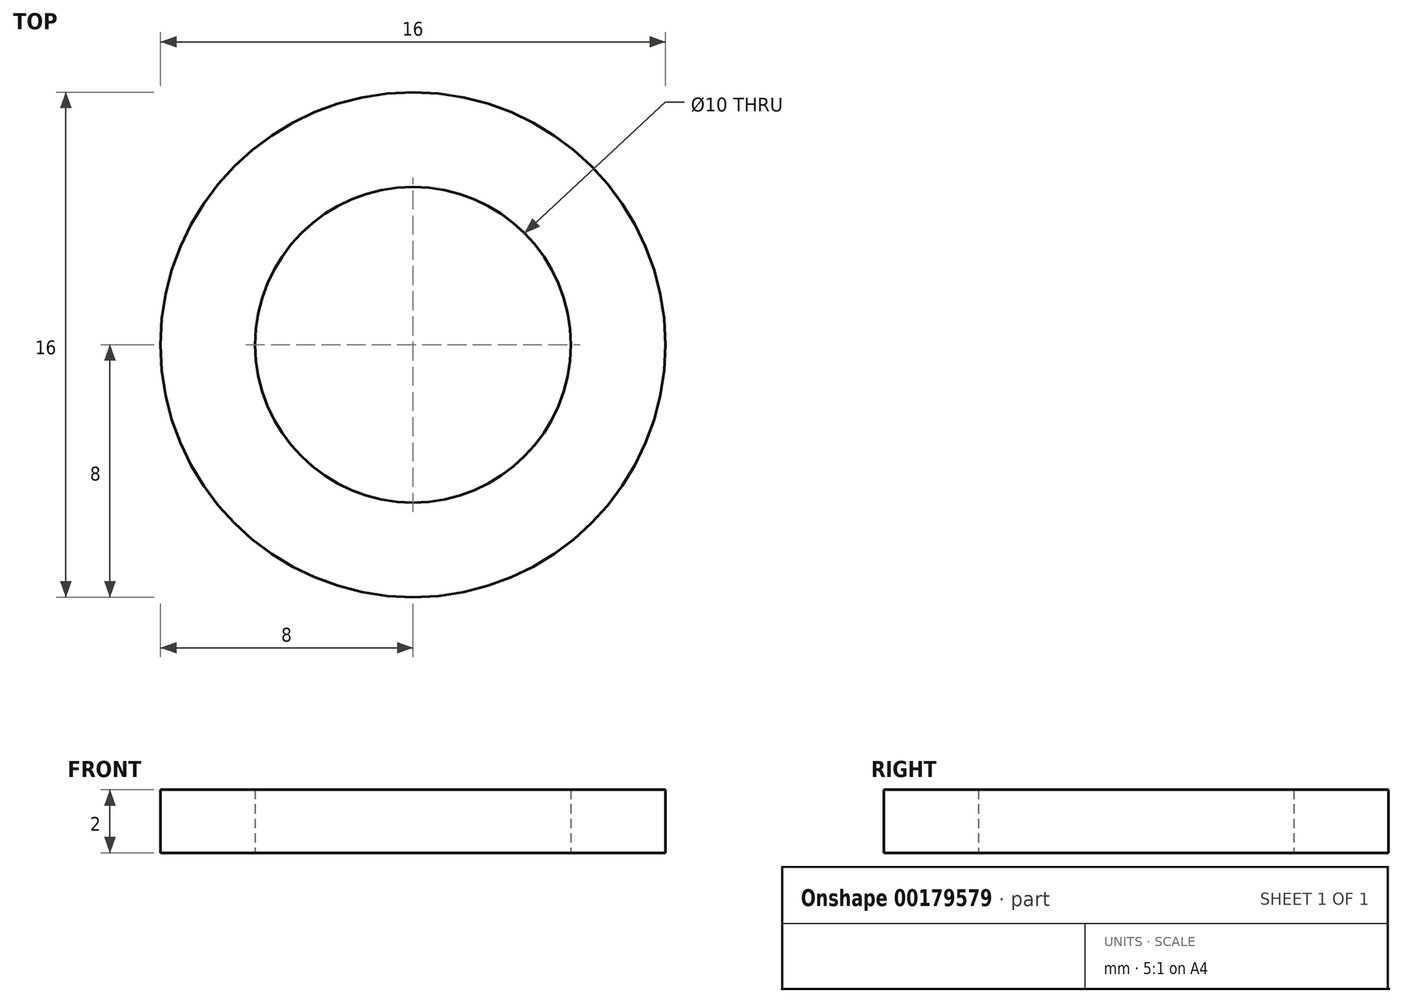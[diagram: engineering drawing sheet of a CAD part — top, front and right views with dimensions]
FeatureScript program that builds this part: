
annotation { "Feature Type Name" : "Feature", "Feature Type Description" : "" }
export const myFeature = defineFeature(function(context is Context, id is Id, definition is map)
    precondition{}
    {
        {
            var Q0;
            Q0=qCreatedBy(makeId("Top.planeOp"),FACE);
            var sketch = newSketch(context, id + "F0", { "sketchPlane" : qUnion([Q0])});
            skCircle(sketch, "E0", {"center": v(0, 0) * mm, "radius": 5 * mm});
            skCircle(sketch, "E1", {"center": v(0, 0) * mm, "radius": 8 * mm});
            skSolve(sketch);
        }
        {
            var Q0;
            Q0=makeQuery(id+"F0.imprint","IMPRINT",FACE,{"disambiguationData":[TD([[makeQuery(id+"F0.imprint","IMPRINT",EDGE,{"derivedFrom":sQuery(id+"F0.wireOp",EDGE,"E0")}),-1.0]])]});
            extrude(context, id + "F1", {"entities" : qUnion([Q0]), "depth" : 2 * mm});
        }
    });
